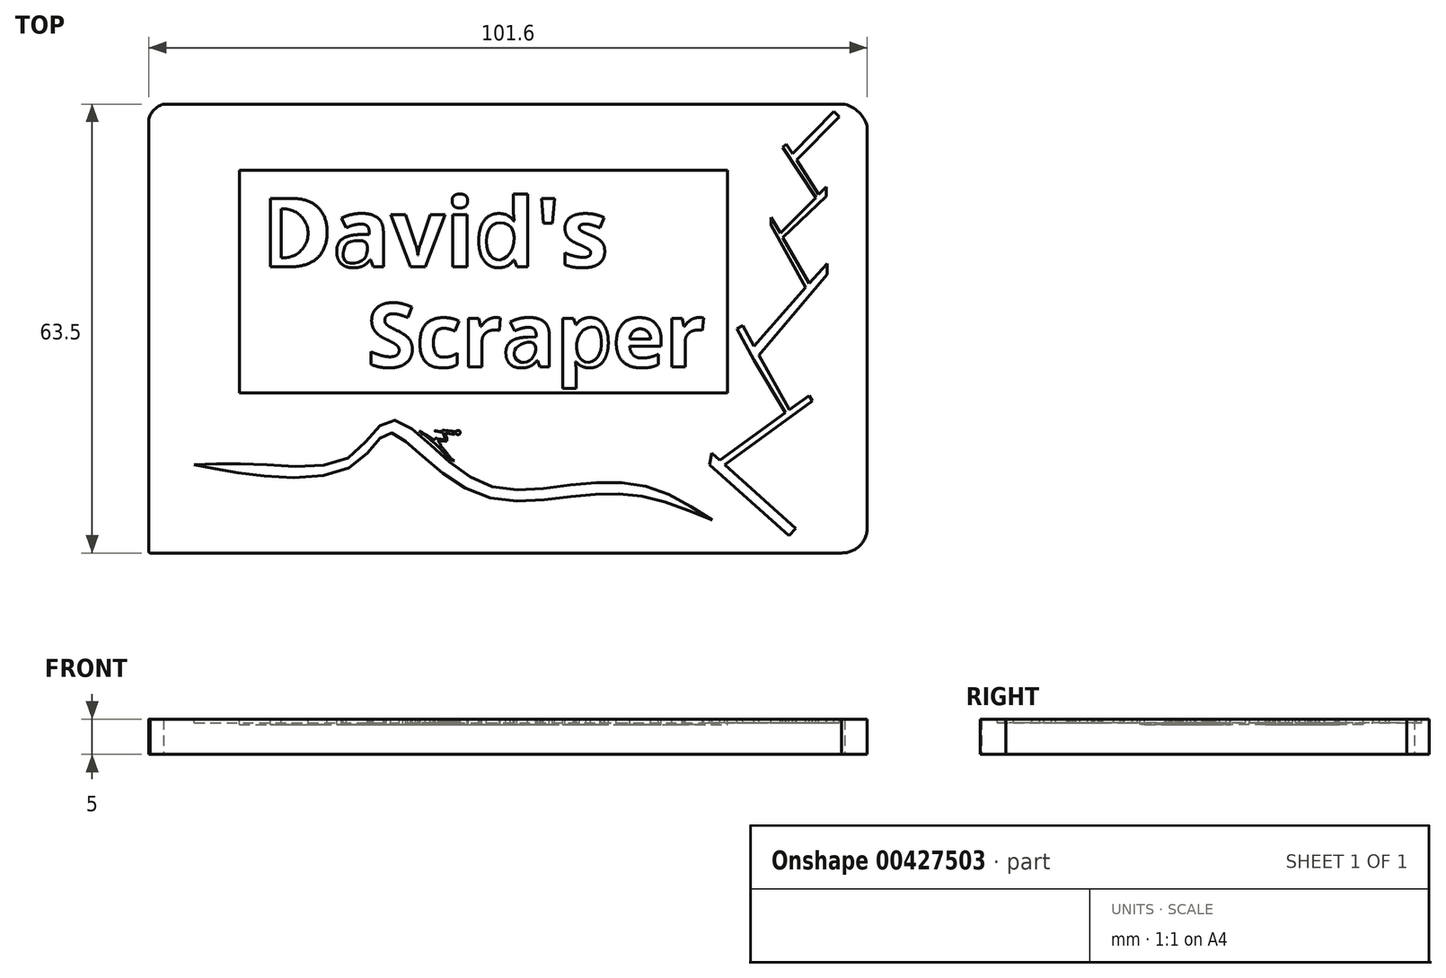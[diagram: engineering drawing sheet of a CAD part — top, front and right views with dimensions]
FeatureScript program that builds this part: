
annotation { "Feature Type Name" : "Feature", "Feature Type Description" : "" }
export const myFeature = defineFeature(function(context is Context, id is Id, definition is map)
    precondition{}
    {
        {
            var Q0;
            Q0=qCreatedBy(makeId("Top.planeOp"),FACE);
            var sketch = newSketch(context, id + "F0", { "sketchPlane" : qUnion([Q0])});
            skLineSegment(sketch, "E0.bottom", {"start": v(2.1, 0) * mm, "end": v(98.44, 0) * mm});
            skLineSegment(sketch, "E0.top", {"start": v(0.18, -63.5) * mm, "end": v(98.16, -63.5) * mm});
            skLineSegment(sketch, "E0.left", {"start": v(0, -2.1) * mm, "end": v(0, -63.32) * mm});
            skLineSegment(sketch, "E0.right", {"start": v(101.6, -3.16) * mm, "end": v(101.6, -60.06) * mm});
            skArc(sketch, "E1", {"start": v(101.6, -3.16) * mm, "mid": v(100.43, -1.17) * mm, "end": v(98.44, 0) * mm});
            skArc(sketch, "E2", {"start": v(2.1, 0) * mm, "mid": v(0.78, -0.78) * mm, "end": v(0, -2.1) * mm});
            skArc(sketch, "E3", {"start": v(98, -63.5) * mm, "mid": v(100.57, -62.47) * mm, "end": v(101.6, -59.9) * mm});
            skArc(sketch, "E4", {"start": v(0, -63.32) * mm, "mid": v(0.05, -63.45) * mm, "end": v(0.18, -63.5) * mm});
            skPoint(sketch, "E5.start.orphan", {"position": v(1.05, -1.05) * mm});
            skSolve(sketch);
        }
        {
            var Q0;
            Q0=qSketchRegion(id+"F0",true);
            extrude(context, id + "F1", {"entities" : qUnion([Q0]), "depth" : 5 * mm});
        }
        {
            var Q0;
            Q0=makeQuery(id+"F1.opExtrude","CAP_FACE",FACE,{"disambiguationData":[OSD([sQuery(id+"F0.wireOp",EDGE,"E0.bottom"),sQuery(id+"F0.wireOp",EDGE,"E0.top"),sQuery(id+"F0.wireOp",EDGE,"E0.left"),sQuery(id+"F0.wireOp",EDGE,"E0.right"),sQuery(id+"F0.wireOp",EDGE,"E1"),sQuery(id+"F0.wireOp",EDGE,"E2"),sQuery(id+"F0.wireOp",EDGE,"E3"),sQuery(id+"F0.wireOp",EDGE,"E4")])],"isStart":false});
            var sketch = newSketch(context, id + "F2", { "sketchPlane" : qUnion([Q0])});
            skLineSegment(sketch, "E6.bottom", {"start": v(12.82, -9.34) * mm, "end": v(81.83, -9.34) * mm});
            skLineSegment(sketch, "E6.top", {"start": v(12.82, -40.88) * mm, "end": v(81.83, -40.88) * mm});
            skLineSegment(sketch, "E6.left", {"start": v(12.82, -9.34) * mm, "end": v(12.82, -40.88) * mm});
            skLineSegment(sketch, "E6.right", {"start": v(81.83, -9.34) * mm, "end": v(81.83, -40.88) * mm});
            skText(sketch, "E7", { "text": "David\'s", "fontName": "OpenSans-Bold.ttf"});
            skText(sketch, "E8", { "text": "Scraper", "fontName": "OpenSans-Bold.ttf"});
            const initialGuessF2  = {"E7": [0.01596, -0.02303, 1, 0, 0.00977], "E8": [0.03084, -0.03721, 1, 0, 0.00907]};
            skSetInitialGuess(sketch, initialGuessF2);
            skSolve(sketch);
        }
        {
            var Q0;
            Q0 = qSketchRegion(id + "F2", true);
            extrude(context, id + "F3", {"entities" : qUnion([Q0]), "operationType" : NewBodyOperationType.REMOVE, "oppositeDirection" : true, "depth" : 0.76 * mm});
        }
        {
            var Q0;
            {var subQ0=sQuery(id+"F0.wireOp",EDGE,"E0.bottom");var subQ1=sQuery(id+"F0.wireOp",EDGE,"E4");var subQ2=sQuery(id+"F0.wireOp",EDGE,"E3");var subQ3=sQuery(id+"F0.wireOp",EDGE,"E2");var subQ4=sQuery(id+"F0.wireOp",EDGE,"E1");var subQ5=sQuery(id+"F0.wireOp",EDGE,"E0.right");var subQ6=sQuery(id+"F0.wireOp",EDGE,"E0.top");var subQ7=sQuery(id+"F0.wireOp",EDGE,"E0.left");Q0=makeQuery(id+"F3.boolean.opBoolean","SPLIT",FACE,{"disambiguationData":[TD([makeQuery(id+"F1.opExtrude","SWEPT_FACE",FACE,{"disambiguationData":[OSD([subQ0])]})])],"derivedFrom":makeQuery(id+"F1.opExtrude","CAP_FACE",FACE,{"disambiguationData":[OSD([subQ0,subQ6,subQ7,subQ5,subQ4,subQ3,subQ2,subQ1])],"isStart":false})});}
            var sketch = newSketch(context, id + "F4", { "sketchPlane" : qUnion([Q0])});
            skLineSegment(sketch, "E9", {"start": v(85.59, -36.24) * mm, "end": v(83.2, -31.76) * mm});
            skLineSegment(sketch, "E10", {"start": v(83.2, -31.76) * mm, "end": v(84.02, -31.32) * mm});
            skLineSegment(sketch, "E11", {"start": v(84.02, -31.32) * mm, "end": v(85.59, -34.27) * mm});
            skLineSegment(sketch, "E12", {"start": v(85.59, -34.27) * mm, "end": v(92.92, -25.97) * mm});
            skPoint(sketch, "E12.startSnap0", {"position": v(85.59, -36.24) * mm});
            skLineSegment(sketch, "E13", {"start": v(95.95, -22.55) * mm, "end": v(95.95, -24.1) * mm});
            skLineSegment(sketch, "E14", {"start": v(95.95, -24.1) * mm, "end": v(86.27, -35.55) * mm});
            skLineSegment(sketch, "E15", {"start": v(85.59, -36.24) * mm, "end": v(90.05, -43.66) * mm});
            skLineSegment(sketch, "E16", {"start": v(90.57, -43.13) * mm, "end": v(86.27, -35.55) * mm});
            skLineSegment(sketch, "E17", {"start": v(93.44, -25.39) * mm, "end": v(89.68, -18.9) * mm});
            skLineSegment(sketch, "E18", {"start": v(88, -16.03) * mm, "end": v(88, -17.13) * mm});
            skLineSegment(sketch, "E19", {"start": v(88, -17.13) * mm, "end": v(92.92, -25.97) * mm});
            skLineSegment(sketch, "E20", {"start": v(89.32, -18.28) * mm, "end": v(94.33, -13.24) * mm});
            skLineSegment(sketch, "E21", {"start": v(95.82, -11.74) * mm, "end": v(95.82, -13.05) * mm});
            skLineSegment(sketch, "E22", {"start": v(95.82, -13.05) * mm, "end": v(89.68, -18.9) * mm});
            skLineSegment(sketch, "E23", {"start": v(94.74, -12.82) * mm, "end": v(91.62, -7.94) * mm});
            skLineSegment(sketch, "E24", {"start": v(90.17, -5.66) * mm, "end": v(89.68, -6.16) * mm});
            skLineSegment(sketch, "E25", {"start": v(89.68, -6.16) * mm, "end": v(94.33, -13.24) * mm});
            skLineSegment(sketch, "E26", {"start": v(91.05, -7.03) * mm, "end": v(96.92, -1.05) * mm});
            skLineSegment(sketch, "E27", {"start": v(96.92, -1.05) * mm, "end": v(97.67, -1.79) * mm});
            skLineSegment(sketch, "E28", {"start": v(97.67, -1.79) * mm, "end": v(91.62, -7.94) * mm});
            skLineSegment(sketch, "E29", {"start": v(93.39, -41.25) * mm, "end": v(80.74, -50.39) * mm});
            skLineSegment(sketch, "E30", {"start": v(81.46, -51.03) * mm, "end": v(81.46, -51.03) * mm});
            skLineSegment(sketch, "E31", {"start": v(81.46, -51.03) * mm, "end": v(93.83, -41.99) * mm});
            skLineSegment(sketch, "E32", {"start": v(93.83, -41.99) * mm, "end": v(93.39, -41.25) * mm});
            skLineSegment(sketch, "E33", {"start": v(79.62, -49.38) * mm, "end": v(80.74, -50.39) * mm});
            skLineSegment(sketch, "E34", {"start": v(91.5, -60.03) * mm, "end": v(90.57, -61.08) * mm});
            skLineSegment(sketch, "E35", {"start": v(90.57, -61.08) * mm, "end": v(79.34, -51.03) * mm});
            skLineSegment(sketch, "E36", {"start": v(79.34, -51.03) * mm, "end": v(79.62, -49.38) * mm});
            skLineSegment(sketch, "E37.trimOffspring", {"start": v(81.46, -51.03) * mm, "end": v(91.5, -60.03) * mm});
            skLineSegment(sketch, "E38.trimOffspring", {"start": v(90.57, -43.3) * mm, "end": v(90.57, -43.13) * mm});
            skPoint(sketch, "E39.trimOffspring.end.orphan", {"position": v(90.57, -44.52) * mm});
            skLineSegment(sketch, "E40.trimOffspring", {"start": v(93.44, -25.39) * mm, "end": v(95.95, -22.55) * mm});
            skLineSegment(sketch, "E41.trimOffspring", {"start": v(89.32, -18.28) * mm, "end": v(88, -16.03) * mm});
            skLineSegment(sketch, "E42.trimOffspring", {"start": v(94.74, -12.82) * mm, "end": v(95.82, -11.74) * mm});
            skLineSegment(sketch, "E43.trimOffspring", {"start": v(91.05, -7.03) * mm, "end": v(90.17, -5.66) * mm});
            skSolve(sketch);
        }
        {
            var Q0;
            Q0=qSketchRegion(id+"F4",true);
            extrude(context, id + "F5", {"entities" : qUnion([Q0]), "operationType" : NewBodyOperationType.REMOVE, "oppositeDirection" : true, "depth" : 0.5 * mm});
        }
        {
            var Q0;
            {var subQ0=sQuery(id+"F0.wireOp",EDGE,"E0.bottom");var subQ1=sQuery(id+"F0.wireOp",EDGE,"E4");var subQ2=sQuery(id+"F0.wireOp",EDGE,"E3");var subQ3=sQuery(id+"F0.wireOp",EDGE,"E2");var subQ4=sQuery(id+"F0.wireOp",EDGE,"E1");var subQ5=sQuery(id+"F0.wireOp",EDGE,"E0.right");var subQ6=sQuery(id+"F0.wireOp",EDGE,"E0.top");var subQ7=sQuery(id+"F0.wireOp",EDGE,"E0.left");Q0=makeQuery(id+"F3.boolean.opBoolean","SPLIT",FACE,{"disambiguationData":[TD([makeQuery(id+"F1.opExtrude","SWEPT_FACE",FACE,{"disambiguationData":[OSD([subQ0])]})])],"derivedFrom":makeQuery(id+"F1.opExtrude","CAP_FACE",FACE,{"disambiguationData":[OSD([subQ0,subQ6,subQ7,subQ5,subQ4,subQ3,subQ2,subQ1])],"isStart":false})});}
            var sketch = newSketch(context, id + "F6", { "sketchPlane" : qUnion([Q0])});
            skFitSpline(sketch, "E44", {"points": [v(6.42, -51) * mm, v(16.15, -51) * mm, v(28.4, -49.9) * mm, v(33.88, -44.74) * mm, v(39.9, -48.29) * mm, v(48.5, -54.1) * mm, v(59.9, -53.88) * mm, v(70.42, -54.1) * mm, v(79.67, -58.82) * mm], "startDerivative": vector(72.85, 2.56) * mm, "endDerivative": vector(69.96, -45.11) * mm});
            skFitSpline(sketch, "E45", {"points": [v(6.42, -51) * mm, v(15.83, -52.59) * mm, v(29.15, -51) * mm, v(33.67, -46.57) * mm, v(37.86, -49.04) * mm, v(47.75, -55.6) * mm, v(60.1, -55.49) * mm, v(69.67, -55.49) * mm, v(79.67, -58.82) * mm], "startDerivative": vector(68.22, -14.71) * mm, "endDerivative": vector(77.09, -31.4) * mm});
            skSolve(sketch);
        }
        {
            var Q0;
            Q0=qSketchRegion(id+"F6",true);
            extrude(context, id + "F7", {"entities" : qUnion([Q0]), "operationType" : NewBodyOperationType.REMOVE, "oppositeDirection" : true, "depth" : 0.5 * mm});
        }
        {
            var Q0;
            {var subQ0=sQuery(id+"F0.wireOp",EDGE,"E0.bottom");var subQ1=sQuery(id+"F0.wireOp",EDGE,"E4");var subQ2=sQuery(id+"F0.wireOp",EDGE,"E3");var subQ3=sQuery(id+"F0.wireOp",EDGE,"E2");var subQ4=sQuery(id+"F0.wireOp",EDGE,"E1");var subQ5=sQuery(id+"F0.wireOp",EDGE,"E0.right");var subQ6=sQuery(id+"F0.wireOp",EDGE,"E0.top");var subQ7=sQuery(id+"F0.wireOp",EDGE,"E0.left");Q0=makeQuery(id+"F3.boolean.opBoolean","SPLIT",FACE,{"disambiguationData":[TD([makeQuery(id+"F1.opExtrude","SWEPT_FACE",FACE,{"disambiguationData":[OSD([subQ0])]})])],"derivedFrom":makeQuery(id+"F1.opExtrude","CAP_FACE",FACE,{"disambiguationData":[OSD([subQ0,subQ6,subQ7,subQ5,subQ4,subQ3,subQ2,subQ1])],"isStart":false})});}
            var sketch = newSketch(context, id + "F8", { "sketchPlane" : qUnion([Q0])});
            skArc(sketch, "E46", {"start": v(42.42, -50.13) * mm, "mid": v(40.48, -48.05) * mm, "end": v(38.26, -46.29) * mm});
            skArc(sketch, "E47", {"start": v(42.42, -50.13) * mm, "mid": v(42.8, -50.35) * mm, "end": v(43.23, -50.45) * mm});
            skArc(sketch, "E48", {"start": v(42.6, -49.97) * mm, "mid": v(41.95, -49.11) * mm, "end": v(41.23, -48.33) * mm});
            skArc(sketch, "E49", {"start": v(42.6, -49.97) * mm, "mid": v(42.89, -50.24) * mm, "end": v(43.23, -50.45) * mm});
            skLineSegment(sketch, "E50", {"start": v(40.31, -47.53) * mm, "end": v(40.49, -47.31) * mm});
            skLineSegment(sketch, "E51", {"start": v(41.97, -47.39) * mm, "end": v(41.57, -46.46) * mm});
            skLineSegment(sketch, "E52", {"start": v(41.75, -46.13) * mm, "end": v(43.5, -46.32) * mm});
            skLineSegment(sketch, "E53", {"start": v(41.98, -47.7) * mm, "end": v(41.04, -47.63) * mm});
            skLineSegment(sketch, "E54", {"start": v(40.95, -47.7) * mm, "end": v(41.22, -48.03) * mm});
            skArc(sketch, "E55", {"start": v(41.23, -48.33) * mm, "mid": v(41.28, -48.18) * mm, "end": v(41.22, -48.03) * mm});
            skLineSegment(sketch, "E56", {"start": v(40.81, -47.31) * mm, "end": v(41.88, -47.48) * mm});
            skArc(sketch, "E57", {"start": v(41.75, -46.13) * mm, "mid": v(41.6, -46.16) * mm, "end": v(41.48, -46.25) * mm});
            skArc(sketch, "E58", {"start": v(41.88, -47.48) * mm, "mid": v(41.95, -47.46) * mm, "end": v(41.97, -47.39) * mm});
            skArc(sketch, "E59", {"start": v(41.98, -47.7) * mm, "mid": v(42.1, -47.67) * mm, "end": v(42.18, -47.56) * mm});
            skArc(sketch, "E60", {"start": v(40.81, -47.31) * mm, "mid": v(40.65, -47.3) * mm, "end": v(40.49, -47.31) * mm});
            skArc(sketch, "E61", {"start": v(41.04, -47.63) * mm, "mid": v(40.98, -47.65) * mm, "end": v(40.95, -47.7) * mm});
            skLineSegment(sketch, "E62", {"start": v(43.53, -46.67) * mm, "end": v(43.5, -46.67) * mm});
            skFitSpline(sketch, "E63", {"points": [v(42.18, -47.56) * mm, v(42.18, -47.4) * mm, v(42.07, -46.96) * mm, v(41.95, -46.63) * mm, v(42.15, -46.58) * mm], "startDerivative": vector(0.04, 0.71) * mm, "endDerivative": vector(1.2, 0.05) * mm});
            skArc(sketch, "E64", {"start": v(43.53, -46.67) * mm, "mid": v(44.04, -46.44) * mm, "end": v(43.5, -46.32) * mm});
            skFitSpline(sketch, "E65", {"points": [v(43.43, -46.58) * mm, v(43.45, -46.84) * mm, v(44.01, -47.07) * mm, v(44.66, -47) * mm, v(44.76, -47) * mm, v(44.75, -47.08) * mm, v(44.01, -47.22) * mm, v(43.33, -46.96) * mm, v(43.28, -46.6) * mm, v(43.43, -46.58) * mm]});
            skArc(sketch, "E66", {"start": v(43.5, -46.67) * mm, "mid": v(43.45, -46.69) * mm, "end": v(43.43, -46.73) * mm});
            skArc(sketch, "E67", {"start": v(43.24, -46.67) * mm, "mid": v(43.23, -46.66) * mm, "end": v(43.2, -46.65) * mm});
            skLineSegment(sketch, "E68.trimOffspring", {"start": v(43.2, -46.65) * mm, "end": v(42.83, -46.62) * mm});
            skLineSegment(sketch, "E69", {"start": v(44.88, -47) * mm, "end": v(43.43, -46.74) * mm});
            skLineSegment(sketch, "E70", {"start": v(42.22, -46.58) * mm, "end": v(43.25, -46.78) * mm});
            skLineSegment(sketch, "E71", {"start": v(44.84, -47.08) * mm, "end": v(44.88, -47) * mm});
            skArc(sketch, "E72", {"start": v(40.49, -46.3) * mm, "mid": v(40.5, -46.28) * mm, "end": v(40.52, -46.25) * mm});
            skPoint(sketch, "E73.start.orphan", {"position": v(40.53, -46.23) * mm});
            skLineSegment(sketch, "E74", {"start": v(41.54, -46.38) * mm, "end": v(40.54, -46.2) * mm});
            skLineSegment(sketch, "E75", {"start": v(41.57, -46.46) * mm, "end": v(40.52, -46.25) * mm});
            skArc(sketch, "E76", {"start": v(40.49, -46.3) * mm, "mid": v(40.5, -46.27) * mm, "end": v(40.51, -46.24) * mm});
            skLineSegment(sketch, "E77", {"start": v(40.53, -46.2) * mm, "end": v(40.46, -46.2) * mm});
            skLineSegment(sketch, "E78", {"start": v(40.46, -46.2) * mm, "end": v(40.51, -46.24) * mm});
            skArc(sketch, "E79.trimOffspring", {"start": v(40.53, -46.2) * mm, "mid": v(40.53, -46.17) * mm, "end": v(40.54, -46.14) * mm});
            skArc(sketch, "E80.trimOffspring", {"start": v(40.54, -46.2) * mm, "mid": v(40.54, -46.17) * mm, "end": v(40.54, -46.14) * mm});
            skLineSegment(sketch, "E81.trimOffspring", {"start": v(41.54, -46.38) * mm, "end": v(41.48, -46.25) * mm});
            skLineSegment(sketch, "E82.trimOffspring", {"start": v(42.22, -46.58) * mm, "end": v(42.15, -46.58) * mm});
            skArc(sketch, "E83.trimOffspring", {"start": v(40.31, -47.53) * mm, "mid": v(39.32, -46.85) * mm, "end": v(38.26, -46.29) * mm});
            skLineSegment(sketch, "E84.trimOffspring", {"start": v(43.24, -46.7) * mm, "end": v(42.83, -46.62) * mm});
            skLineSegment(sketch, "E85.trimOffspring", {"start": v(43.44, -46.82) * mm, "end": v(44.52, -47.02) * mm});
            skLineSegment(sketch, "E86.trimOffspring", {"start": v(44.76, -47.07) * mm, "end": v(44.84, -47.08) * mm});
            skSolve(sketch);
        }
        {
            var Q0;
            Q0=makeQuery(id+"F8.imprint","IMPRINT",FACE,{"disambiguationData":[TD([[makeQuery(id+"F8.imprint","IMPRINT",EDGE,{"derivedFrom":sQuery(id+"F8.wireOp",EDGE,"E46")}),-1.0]])]});
            extrude(context, id + "F9", {"entities" : qUnion([Q0]), "operationType" : NewBodyOperationType.REMOVE, "oppositeDirection" : true, "depth" : 0.5 * mm});
        }
        {
            var Q0;
            Q0=makeQuery(id+"F3.boolean.opBoolean","SPLIT",FACE,{"disambiguationData":[TD([makeQuery(id+"F3.opExtrude","SWEPT_FACE",FACE,{"disambiguationData":[OSD([sQuery(id+"F2.wireOp",EDGE,"E7.sketch_text.stroke-0")])]})])],"derivedFrom":makeQuery(id+"F1.opExtrude","CAP_FACE",FACE,{"disambiguationData":[OSD([sQuery(id+"F0.wireOp",EDGE,"E0.bottom"),sQuery(id+"F0.wireOp",EDGE,"E0.top"),sQuery(id+"F0.wireOp",EDGE,"E0.left"),sQuery(id+"F0.wireOp",EDGE,"E0.right"),sQuery(id+"F0.wireOp",EDGE,"E1"),sQuery(id+"F0.wireOp",EDGE,"E2"),sQuery(id+"F0.wireOp",EDGE,"E3"),sQuery(id+"F0.wireOp",EDGE,"E4")])],"isStart":false})});
            var sketch = newSketch(context, id + "F10", { "sketchPlane" : qUnion([Q0])});
            skLineSegment(sketch, "E87", {"start": v(18.73, -14.83) * mm, "end": v(18.73, -21.75) * mm});
            skArc(sketch, "E88", {"start": v(18.73, -21.75) * mm, "mid": v(22.53, -18.3) * mm, "end": v(18.73, -14.83) * mm});
            skFitSpline(sketch, "E89", {"points": [v(30.62, -19.52) * mm, v(28.45, -19.52) * mm, v(27.7, -20.22) * mm, v(27.8, -22.22) * mm, v(30.15, -22.16) * mm, v(30.86, -20.99) * mm, v(30.62, -19.52) * mm]});
            skFitSpline(sketch, "E90", {"points": [v(51.3, -17.5) * mm, v(51.23, -20.82) * mm, v(49.57, -22.06) * mm, v(48.16, -21.23) * mm, v(48, -18) * mm, v(49.32, -16.84) * mm, v(51.3, -17.5) * mm]});
            skFitSpline(sketch, "E91", {"points": [v(54.36, -33.83) * mm, v(52.2, -34.29) * mm, v(51.7, -35.66) * mm, v(52.9, -36.57) * mm, v(54.57, -35.45) * mm, v(54.36, -33.83) * mm]});
            skFitSpline(sketch, "E92", {"points": [v(61, -32.47) * mm, v(60.81, -35.72) * mm, v(62.24, -36.51) * mm, v(63.62, -35.57) * mm, v(63.97, -33.2) * mm, v(63.18, -31.58) * mm, v(61, -32.47) * mm]});
            skLineSegment(sketch, "E93", {"start": v(68.06, -33.22) * mm, "end": v(70.97, -33.22) * mm});
            skArc(sketch, "E94", {"start": v(70.97, -33.22) * mm, "mid": v(69.52, -31.8) * mm, "end": v(68.06, -33.22) * mm});
            skSolve(sketch);
        }
        {
            var Q0;
            Q0=makeQuery(id+"F10.imprint","IMPRINT",FACE,{"disambiguationData":[TD([[makeQuery(id+"F10.imprint","IMPRINT",EDGE,{"derivedFrom":sQuery(id+"F10.wireOp",EDGE,"E87")}),1.0]])]});
            var Q1;
            Q1=makeQuery(id+"F10.imprint","IMPRINT",FACE,{"disambiguationData":[TD([[makeQuery(id+"F10.imprint","IMPRINT",EDGE,{"derivedFrom":sQuery(id+"F10.wireOp",EDGE,"E89")}),1.0]])]});
            var Q2;
            Q2=makeQuery(id+"F10.imprint","IMPRINT",FACE,{"disambiguationData":[TD([[makeQuery(id+"F10.imprint","IMPRINT",EDGE,{"derivedFrom":sQuery(id+"F10.wireOp",EDGE,"E90")}),-1.0]])]});
            var Q3;
            Q3=makeQuery(id+"F10.imprint","IMPRINT",FACE,{"disambiguationData":[TD([[makeQuery(id+"F10.imprint","IMPRINT",EDGE,{"derivedFrom":sQuery(id+"F10.wireOp",EDGE,"E91")}),1.0]])]});
            var Q4;
            Q4=makeQuery(id+"F10.imprint","IMPRINT",FACE,{"disambiguationData":[TD([[makeQuery(id+"F10.imprint","IMPRINT",EDGE,{"derivedFrom":sQuery(id+"F10.wireOp",EDGE,"E92")}),1.0]])]});
            var Q5;
            Q5=makeQuery(id+"F10.imprint","IMPRINT",FACE,{"disambiguationData":[TD([[makeQuery(id+"F10.imprint","IMPRINT",EDGE,{"derivedFrom":sQuery(id+"F10.wireOp",EDGE,"E93")}),1.0]])]});
            extrude(context, id + "F11", {"entities" : qUnion([Q0, Q1, Q2, Q3, Q4, Q5]), "operationType" : NewBodyOperationType.REMOVE, "oppositeDirection" : true, "depth" : 0.76 * mm});
        }
    });
